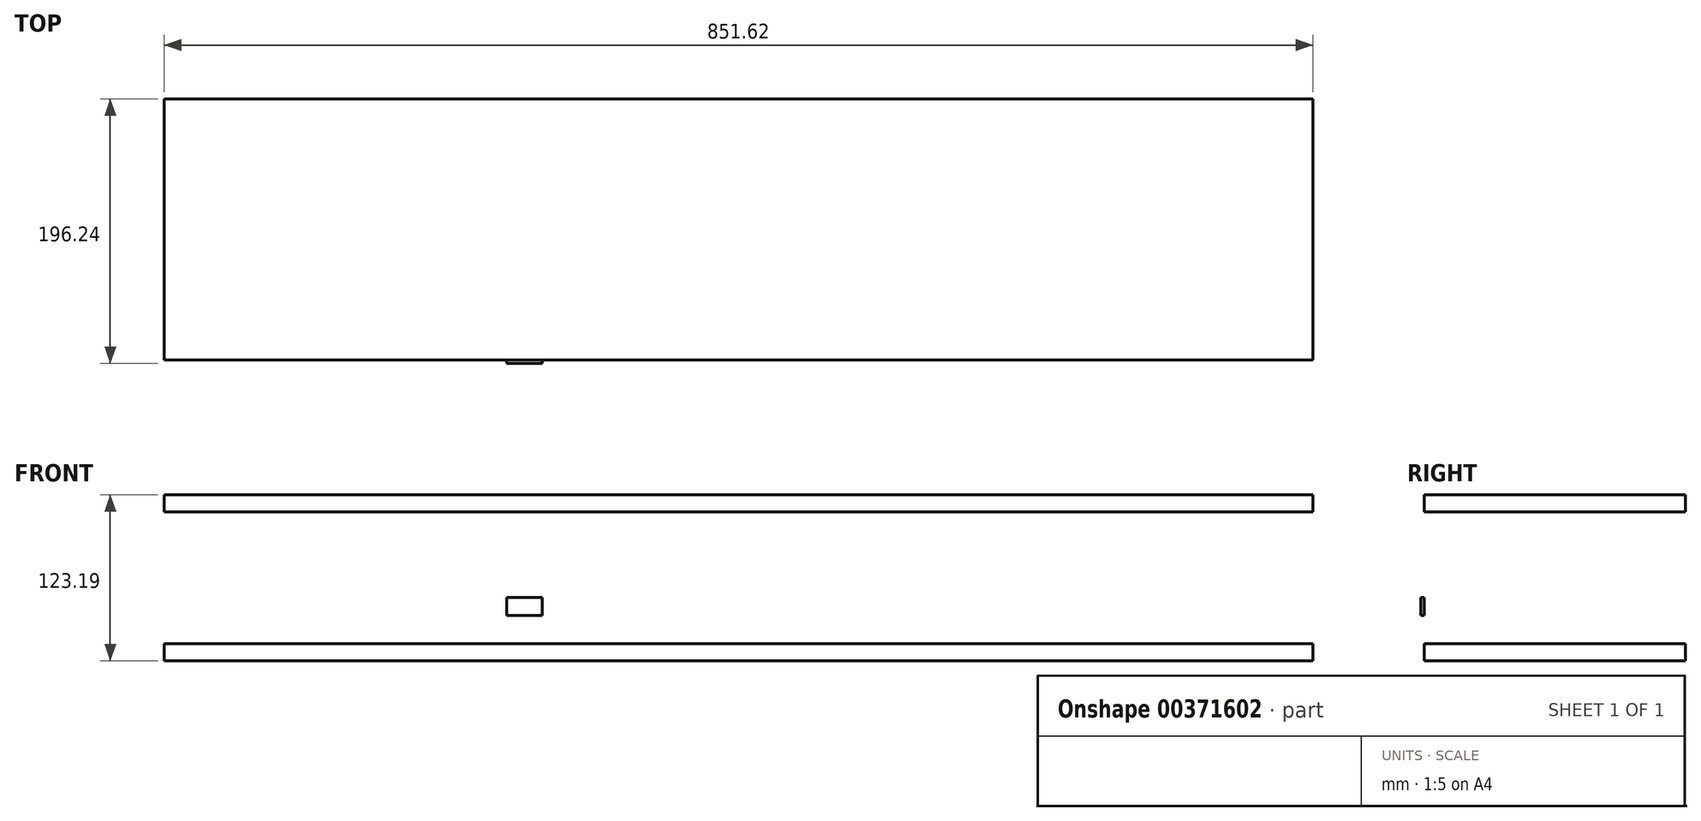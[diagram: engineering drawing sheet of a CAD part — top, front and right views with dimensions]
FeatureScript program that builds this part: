
annotation { "Feature Type Name" : "Feature", "Feature Type Description" : "" }
export const myFeature = defineFeature(function(context is Context, id is Id, definition is map)
    precondition{}
    {
        {
            var Q0;
            Q0=qCreatedBy(makeId("Top.planeOp"),FACE);
            var sketch = newSketch(context, id + "F0", { "sketchPlane" : qUnion([Q0])});
            skLineSegment(sketch, "E0.bottom", {"start": v(-315.05, 193.7) * mm, "end": v(536.57, 193.7) * mm});
            skLineSegment(sketch, "E0.top", {"start": v(-315.05, 0) * mm, "end": v(536.57, 0) * mm});
            skLineSegment(sketch, "E0.left", {"start": v(-315.05, 193.7) * mm, "end": v(-315.05, 0) * mm});
            skLineSegment(sketch, "E0.right", {"start": v(536.57, 193.7) * mm, "end": v(536.57, 0) * mm});
            skSolve(sketch);
        }
        {
            var Q0;
            Q0=makeQuery(id+"F0.imprint","IMPRINT",FACE,{"disambiguationData":[TD([[makeQuery(id+"F0.imprint","IMPRINT",EDGE,{"derivedFrom":sQuery(id+"F0.wireOp",EDGE,"E0.bottom")}),-1.0]])]});
            extrude(context, id + "F1", {"entities" : qUnion([Q0]), "depth" : 12.7 * mm});
        }
        {
            var Q0;
            Q0=makeQuery(id+"F1.opExtrude","SWEPT_BODY",BODY,{"disambiguationData":[OSD([sQuery(id+"F0.wireOp",EDGE,"E0.bottom"),sQuery(id+"F0.wireOp",EDGE,"E0.top"),sQuery(id+"F0.wireOp",EDGE,"E0.left"),sQuery(id+"F0.wireOp",EDGE,"E0.right")])]});
            transform(context, id + "F2", {"entities" : qUnion([Q0]), "transformType" : TransformType.TRANSLATION_3D, "dx" : 0 * mm, "dy" : 0 * mm, "dz" : 110.49 * mm, "makeCopy" : true});
        }
        {
            var Q0;
            Q0=qCreatedBy(makeId("Top.planeOp"),FACE);
            var sketch = newSketch(context, id + "F3", { "sketchPlane" : qUnion([Q0])});
            skLineSegment(sketch, "E1.bottom", {"start": v(-317.53, 0) * mm, "end": v(537.84, 0) * mm});
            skLineSegment(sketch, "E1.top", {"start": v(-317.53, -194.67) * mm, "end": v(537.84, -194.67) * mm});
            skLineSegment(sketch, "E1.left", {"start": v(-317.53, 0) * mm, "end": v(-317.53, -194.67) * mm});
            skLineSegment(sketch, "E1.right", {"start": v(537.84, 0) * mm, "end": v(537.84, -194.67) * mm});
            skSolve(sketch);
        }
        {
            var Q0;
            Q0=makeQuery(id+"F3.imprint","IMPRINT",FACE,{"disambiguationData":[TD([[makeQuery(id+"F3.imprint","IMPRINT",EDGE,{"derivedFrom":sQuery(id+"F3.wireOp",EDGE,"E1.bottom")}),-1.0]])]});
            extrude(context, id + "F4", {"entities" : qUnion([Q0]), "depth" : 12.7 * mm});
        }
        {
            var Q0;
            Q0=makeQuery(id+"F4.opExtrude","SWEPT_BODY",BODY,{"disambiguationData":[OSD([sQuery(id+"F3.wireOp",EDGE,"E1.bottom"),sQuery(id+"F3.wireOp",EDGE,"E1.top"),sQuery(id+"F3.wireOp",EDGE,"E1.left"),sQuery(id+"F3.wireOp",EDGE,"E1.right")])]});
            deleteBodies(context, id + "F5", {"entities" : qUnion([Q0])});
        }
        {
            var Q0;
            Q0=qCreatedBy(makeId("Front.planeOp"),FACE);
            var sketch = newSketch(context, id + "F6", { "sketchPlane" : qUnion([Q0])});
            skLineSegment(sketch, "E2.bottom", {"start": v(-61.03, 33.85) * mm, "end": v(-34.95, 33.85) * mm});
            skLineSegment(sketch, "E2.top", {"start": v(-61.03, 46.89) * mm, "end": v(-34.95, 46.89) * mm});
            skLineSegment(sketch, "E2.left", {"start": v(-61.03, 33.85) * mm, "end": v(-61.03, 46.89) * mm});
            skLineSegment(sketch, "E2.right", {"start": v(-34.95, 33.85) * mm, "end": v(-34.95, 46.89) * mm});
            skSolve(sketch);
        }
        {
            var Q0;
            Q0=makeQuery(id+"F6.imprint","IMPRINT",FACE,{"disambiguationData":[TD([[makeQuery(id+"F6.imprint","IMPRINT",EDGE,{"derivedFrom":sQuery(id+"F6.wireOp",EDGE,"E2.bottom")}),1.0]])]});
            extrude(context, id + "F7", {"entities" : qUnion([Q0]), "depth" : 2.54 * mm});
        }
    });
